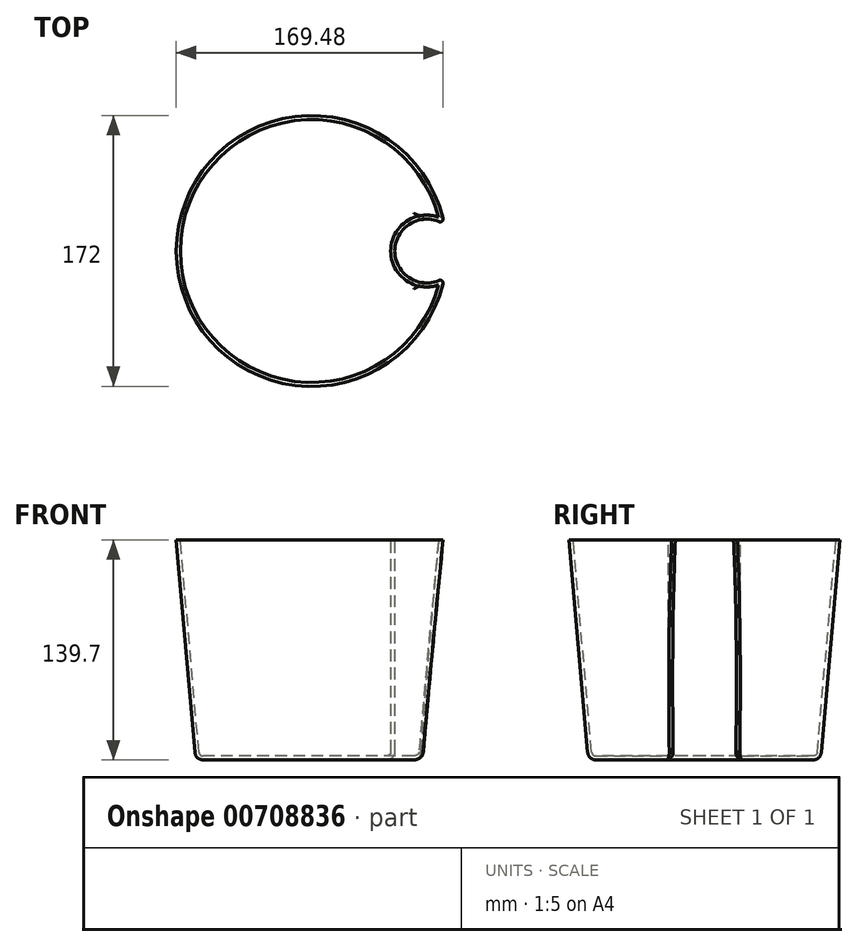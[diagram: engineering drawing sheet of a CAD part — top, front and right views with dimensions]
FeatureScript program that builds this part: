
annotation { "Feature Type Name" : "Feature", "Feature Type Description" : "" }
export const myFeature = defineFeature(function(context is Context, id is Id, definition is map)
    precondition{}
    {
        {
            var Q0;
            Q0=qCreatedBy(makeId("Top.planeOp"),FACE);
            var sketch = newSketch(context, id + "F0", { "sketchPlane" : qUnion([Q0])});
            skCircle(sketch, "E0", {"center": v(0, 0) * mm, "radius": 86 * mm});
            skSolve(sketch);
        }
        {
            var Q0;
            Q0 = qSketchRegion(id + "F0", true);
            var Q1;
            Q1=makeQuery(id+"F0.imprint","IMPRINT",FACE,{"disambiguationData":[TD([[makeQuery(id+"F0.imprint","IMPRINT",EDGE,{"derivedFrom":sQuery(id+"F0.wireOp",EDGE,"E0")}),1.0]])]});
            extrude(context, id + "F1", {"entities" : qUnion([Q0, Q1]), "oppositeDirection" : true, "depth" : 139.7 * mm, "offsetDistance" : 25.4 * mm, "hasDraft" : true, "draftAngle" : 5 * degree, "draftPullDirection" : true});
        }
        {
            var Q0;
            Q0=qCreatedBy(makeId("Top.planeOp"),FACE);
            var sketch = newSketch(context, id + "F2", { "sketchPlane" : qUnion([Q0])});
            skCircle(sketch, "E1", {"center": v(73, 0) * mm, "radius": 20.25 * mm});
            skSolve(sketch);
        }
        {
            var Q0;
            Q0=makeQuery(id+"F2.imprint","IMPRINT",FACE,{"disambiguationData":[TD([[makeQuery(id+"F2.imprint","IMPRINT",EDGE,{"derivedFrom":sQuery(id+"F2.wireOp",EDGE,"E1")}),1.0]])]});
            extrude(context, id + "F3", {"entities" : qUnion([Q0]), "operationType" : NewBodyOperationType.REMOVE, "endBound" : BoundingType.THROUGH_ALL, "oppositeDirection" : true, "depth" : 25.4 * mm, "offsetDistance" : 25.4 * mm});
        }
        {
            var Q0;
            Q0=makeQuery(id+"F3.boolean.opBoolean","INTERSECT",EDGE,{"disambiguationData":[OD(1.0)],"derivedFrom":[makeQuery(id+"F1.opExtrude","SWEPT_FACE",FACE,{"disambiguationData":[OSD([sQuery(id+"F0.wireOp",EDGE,"E0")])]}),makeQuery(id+"F3.opExtrude","SWEPT_FACE",FACE,{"disambiguationData":[OSD([sQuery(id+"F2.wireOp",EDGE,"E1")])]})]});
            var Q1;
            Q1=makeQuery(id+"F3.boolean.opBoolean","INTERSECT",EDGE,{"disambiguationData":[OD(0.0)],"derivedFrom":[makeQuery(id+"F1.opExtrude","SWEPT_FACE",FACE,{"disambiguationData":[OSD([sQuery(id+"F0.wireOp",EDGE,"E0")])]}),makeQuery(id+"F3.opExtrude","SWEPT_FACE",FACE,{"disambiguationData":[OSD([sQuery(id+"F2.wireOp",EDGE,"E1")])]})]});
            fillet(context, id + "F4", {"entities" : qUnion([Q0, Q1]), "radius" : 1.9 * mm, "tangentPropagation" : true, "allowEdgeOverflow" : false});
        }
        {
            var Q0;
            Q0=makeQuery(id+"F1.opExtrude","CAP_EDGE",EDGE,{"disambiguationData":[OSD([sQuery(id+"F0.wireOp",EDGE,"E0")])],"isStart":false});
            fillet(context, id + "F5", {"entities" : qUnion([Q0]), "radius" : 5.08 * mm, "tangentPropagation" : true, "allowEdgeOverflow" : false});
        }
        {
            var Q0;
            Q0=makeQuery(id+"F1.opExtrude","CAP_FACE",FACE,{"disambiguationData":[OSD([sQuery(id+"F0.wireOp",EDGE,"E0")])],"isStart":true});
            shell(context, id + "F6", {"entities" : qUnion([Q0]), "thickness" : 2.54 * mm});
        }
    });
